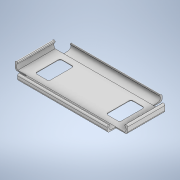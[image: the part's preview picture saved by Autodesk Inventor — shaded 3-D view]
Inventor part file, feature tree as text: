
AUTODESK INVENTOR PART (.ipt)
format: ipt  version: 2020 (Build 240168000, 168)  size: 346,624 bytes
history: native  units: mm
features: sketch x5, extrude x5, fillet x2, projected_geometry x1
ambient origin geometry x8: Origin, YZ Plane, XZ Plane, XY Plane, X Axis, Y Axis, Z Axis, Center Point
bodies: Body1 (feature_tree)
feature tree (13):
  sketch  "Sketch1"  dims[d0=9.5mm d1=11.770907mm]
  sketch  "Sketch2"  dims[d2=50.25602mm d3=63.323636mm]
  extrude  "Extrusion2"  Depth=11.770907mm
  extrude  "Extrusion3"  Depth=63.323636mm
  extrude  "Extrusion4"  Depth=7.278553mm
  extrude  "Extrusion5"  Depth=10.178962mm
  fillet  "Fillet1"  Radius=3.006362mm
  fillet  "Fillet2"  Radius=0.381374mm
  extrude  "Extrusion6"  TaperAngle=90.0deg  [1 undecoded]
  sketch  "Sketch3"  dims[d4=7.543377mm d5=7.278553mm]
  sketch  "Sketch4"  dims[d6=13.530576mm d7=10.178962mm d8=3.006362mm d9=0.381374mm]
  sketch  "Sketch8"  dims[d10=8.152475mm d11=90.0deg d12=90.0deg d13=182.762823mm d14=213.345323mm d15=82.749834mm d16=838.251776mm d17=23.985455mm d18=5.035479mm d19=70.066536mm d20=146.705902mm d21=189.528499mm d22=164.68023mm d23=138.415323mm d24=527.101779mm d25=255.80879mm d26=252.614765mm d27=215.951781mm d28=299.08508mm d31=30.0mm d32=33.429929mm d33=50.290385mm d34=63.798039mm d35=8.713599mm d36=18.996342mm d37=3.705985mm d38=4.3568mm d39=21.494574mm d40=1.207753mm d41=4.3568mm d42=7.886471mm d43=0.827129mm d44=4.3568mm d45=1.724373mm d46=6.989226mm d47=3.990886mm d48=12.704485mm d49=3.182814mm d50=11.896413mm d51=20.064763mm d52=3764.948058mm d53=16.37444mm d54=3289.717798mm d55=57.303624mm d56=2466.944268mm d57=59.093716mm d58=46.781222mm d59=3049.802442mm d60=59.093716mm d61=26.771897mm d62=3395.170192mm d63=59.093716mm d64=58.821879mm d65=3579.956247mm d66=158.18518mm d67=2606.435143mm d68=239.777909mm d69=195.409915mm d70=2853.836078mm d71=3289.717798mm d72=16.37444mm d73=3256.109492mm d74=3256.109492mm d75=45.25763mm d76=220.265324mm d77=3276.809698mm d78=3312.698463mm d79=3281.475519mm d80=153.35556mm d81=3202.045193mm d82=1535.478941mm d83=30.0mm d84=0.0mm d85=3000.0mm d86=0.0mm d87=1250.0mm d88=0.0mm d90=420.0mm d91=420.0mm d92=460.0mm d93=471.0mm d94=1200.0mm d95=0.0mm d96=63.5mm d97=15.0mm d98=956.474029mm d99=956.474029mm d100=460.0mm d107=187.0mm d108=0.0mm]
  projected_geometry  "Projected Loop1"
note: 1 required parameter value undecoded (feature->parameter linkage not recoverable at this tier; creation-order binding heuristic only, values carry confidence <= 0.55)
